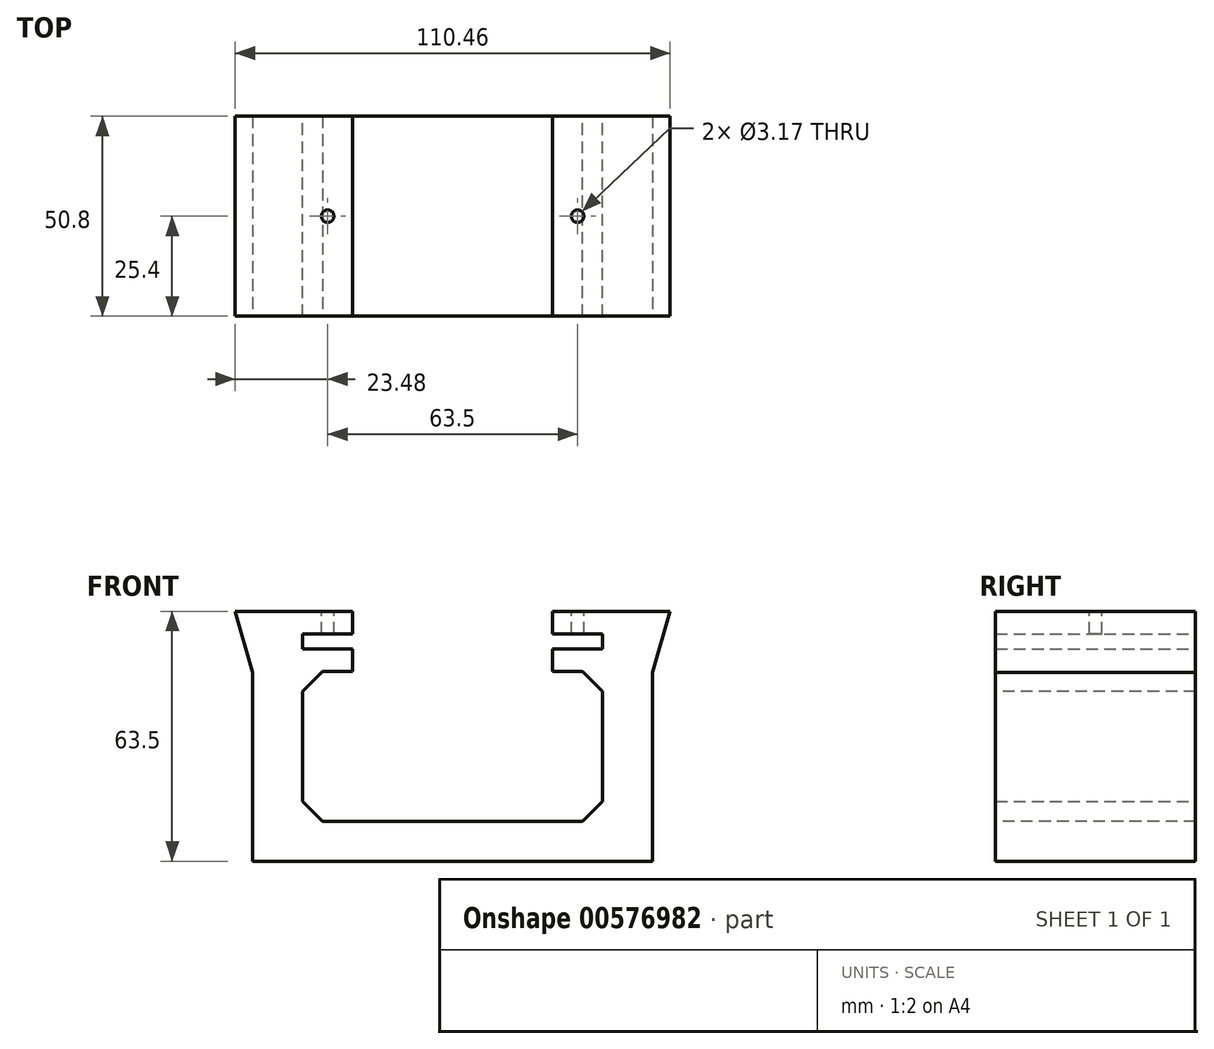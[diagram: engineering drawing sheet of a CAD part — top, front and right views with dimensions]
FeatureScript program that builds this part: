
annotation { "Feature Type Name" : "Feature", "Feature Type Description" : "" }
export const myFeature = defineFeature(function(context is Context, id is Id, definition is map)
    precondition{}
    {
        {
            var Q0;
            Q0=qCreatedBy(makeId("Front.planeOp"),FACE);
            var sketch = newSketch(context, id + "F0", { "sketchPlane" : qUnion([Q0])});
            skLineSegment(sketch, "E0.bottom", {"start": v(0, 0) * mm, "end": v(101.6, 0) * mm, "construction": true});
            skLineSegment(sketch, "E0.top", {"start": v(0, 63.5) * mm, "end": v(101.6, 63.5) * mm, "construction": true});
            skLineSegment(sketch, "E0.left", {"start": v(0, 0) * mm, "end": v(0, 63.5) * mm, "construction": true});
            skLineSegment(sketch, "E0.right", {"start": v(101.6, 0) * mm, "end": v(101.6, 63.5) * mm, "construction": true});
            skPoint(sketch, "E1", {"position": v(50.8, 63.5) * mm});
            skPoint(sketch, "E2", {"position": v(50.8, 0) * mm});
            skLineSegment(sketch, "E3", {"start": v(50.8, 63.5) * mm, "end": v(50.8, 0) * mm, "construction": true});
            skLineSegment(sketch, "E4.bottom", {"start": v(88.9, 53.98) * mm, "end": v(12.7, 53.97) * mm, "construction": true});
            skLineSegment(sketch, "E4.top", {"start": v(88.9, 57.79) * mm, "end": v(12.7, 57.79) * mm, "construction": true});
            skLineSegment(sketch, "E4.left", {"start": v(88.9, 53.98) * mm, "end": v(88.9, 57.79) * mm, "construction": true});
            skLineSegment(sketch, "E4.right", {"start": v(12.7, 53.97) * mm, "end": v(12.7, 57.79) * mm, "construction": true});
            skPoint(sketch, "E4.middle", {"position": v(50.8, 55.88) * mm});
            skLineSegment(sketch, "E5", {"start": v(25.4, 63.5) * mm, "end": v(25.4, 0) * mm, "construction": true});
            skLineSegment(sketch, "E6", {"start": v(0, 48.26) * mm, "end": v(101.6, 48.26) * mm, "construction": true});
            skLineSegment(sketch, "E7", {"start": v(25.4, 63.5) * mm, "end": v(0, 63.5) * mm});
            skLineSegment(sketch, "E8", {"start": v(0, 0) * mm, "end": v(50.8, 0) * mm});
            skLineSegment(sketch, "E9", {"start": v(50.8, 10.16) * mm, "end": v(12.7, 10.16) * mm});
            skLineSegment(sketch, "E10", {"start": v(12.7, 10.16) * mm, "end": v(12.7, 48.26) * mm});
            skLineSegment(sketch, "E11", {"start": v(12.7, 48.26) * mm, "end": v(25.4, 48.26) * mm});
            skLineSegment(sketch, "E12", {"start": v(25.4, 48.26) * mm, "end": v(25.4, 53.97) * mm});
            skLineSegment(sketch, "E13", {"start": v(25.4, 53.97) * mm, "end": v(12.7, 53.97) * mm});
            skLineSegment(sketch, "E14", {"start": v(12.7, 57.79) * mm, "end": v(25.4, 57.79) * mm});
            skLineSegment(sketch, "E15", {"start": v(25.4, 57.79) * mm, "end": v(25.4, 63.5) * mm});
            skLineSegment(sketch, "E16", {"start": v(12.7, 57.79) * mm, "end": v(12.7, 53.97) * mm});
            skLineSegment(sketch, "E17.MirrorCS", {"start": v(88.9, 53.97) * mm, "end": v(88.9, 57.78) * mm, "construction": true});
            skLineSegment(sketch, "E18.MirrorCS", {"start": v(88.9, 48.26) * mm, "end": v(76.2, 48.26) * mm});
            skLineSegment(sketch, "E19.MirrorCS", {"start": v(88.9, 10.16) * mm, "end": v(88.9, 48.26) * mm});
            skLineSegment(sketch, "E20.MirrorCS", {"start": v(76.2, 48.26) * mm, "end": v(76.2, 53.97) * mm});
            skLineSegment(sketch, "E21.MirrorCS", {"start": v(76.2, 53.97) * mm, "end": v(88.9, 53.97) * mm});
            skLineSegment(sketch, "E22.MirrorCS", {"start": v(50.8, 10.16) * mm, "end": v(88.9, 10.16) * mm});
            skLineSegment(sketch, "E23.MirrorCS", {"start": v(88.9, 57.78) * mm, "end": v(76.2, 57.78) * mm});
            skLineSegment(sketch, "E24.MirrorCS", {"start": v(88.9, 57.78) * mm, "end": v(88.9, 53.97) * mm});
            skLineSegment(sketch, "E25.MirrorCS", {"start": v(76.2, 57.78) * mm, "end": v(76.2, 63.5) * mm});
            skLineSegment(sketch, "E26.MirrorCS", {"start": v(101.6, 0) * mm, "end": v(50.8, 0) * mm});
            skLineSegment(sketch, "E27.MirrorCS", {"start": v(76.2, 63.5) * mm, "end": v(101.6, 63.5) * mm});
            skLineSegment(sketch, "E28.MirrorCS", {"start": v(76.2, 63.5) * mm, "end": v(76.2, 0) * mm, "construction": true});
            skLineSegment(sketch, "E29", {"start": v(0, 63.5) * mm, "end": v(0, 0) * mm});
            skLineSegment(sketch, "E30", {"start": v(101.6, 63.5) * mm, "end": v(101.6, 0) * mm});
            skSolve(sketch);
        }
        {
            var Q0;
            Q0=makeQuery(id+"F0.imprint","IMPRINT",FACE,{"disambiguationData":[TD([[makeQuery(id+"F0.imprint","IMPRINT",EDGE,{"derivedFrom":sQuery(id+"F0.wireOp",EDGE,"E7")}),1.0]])]});
            extrude(context, id + "F1", {"entities" : qUnion([Q0]), "depth" : 50.8 * mm, "offsetDistance" : 25.4 * mm});
        }
        {
            var Q0;
            Q0=makeQuery(id+"F1.opExtrude","SWEPT_FACE",FACE,{"disambiguationData":[OSD([sQuery(id+"F0.wireOp",EDGE,"E7")])]});
            var sketch = newSketch(context, id + "F2", { "sketchPlane" : qUnion([Q0])});
            skLineSegment(sketch, "E31", {"start": v(12.7, 0) * mm, "end": v(12.7, -50.8) * mm, "construction": true});
            skLineSegment(sketch, "E32", {"start": v(50.8, 0) * mm, "end": v(50.8, -50.58) * mm, "construction": true});
            skLineSegment(sketch, "E33", {"start": v(12.7, 0) * mm, "end": v(25.4, 0) * mm, "construction": true});
            skPoint(sketch, "E34", {"position": v(19.05, 0) * mm});
            skLineSegment(sketch, "E35", {"start": v(12.7, -50.8) * mm, "end": v(25.4, -50.8) * mm, "construction": true});
            skPoint(sketch, "E36", {"position": v(19.05, -50.8) * mm});
            skLineSegment(sketch, "E37", {"start": v(19.05, 0) * mm, "end": v(19.05, -50.8) * mm, "construction": true});
            skPoint(sketch, "E38", {"position": v(19.05, -25.4) * mm});
            skCircle(sketch, "E39", {"center": v(19.05, -25.4) * mm, "radius": 1.59 * mm});
            skCircle(sketch, "E40.MirrorC", {"center": v(82.55, -25.4) * mm, "radius": 1.59 * mm});
            skSolve(sketch);
        }
        {
            var Q0;
            Q0 = qSketchRegion(id + "F2", true);
            extrude(context, id + "F3", {"entities" : qUnion([Q0]), "operationType" : NewBodyOperationType.REMOVE, "endBound" : BoundingType.UP_TO_NEXT, "oppositeDirection" : true, "depth" : 25.4 * mm, "offsetDistance" : 25.4 * mm});
        }
        {
            var Q0;
            Q0=makeQuery(id+"F1.opExtrude","SWEPT_EDGE",EDGE,{"disambiguationData":[OSD([sQuery(id+"F0.wireOp",EDGE,"E9"),sQuery(id+"F0.wireOp",EDGE,"E10")])]});
            var Q1;
            Q1=makeQuery(id+"F1.opExtrude","SWEPT_EDGE",EDGE,{"disambiguationData":[OSD([sQuery(id+"F0.wireOp",EDGE,"E19.MirrorCS"),sQuery(id+"F0.wireOp",EDGE,"E22.MirrorCS")])]});
            var Q2;
            Q2=makeQuery(id+"F1.opExtrude","SWEPT_EDGE",EDGE,{"disambiguationData":[OSD([sQuery(id+"F0.wireOp",EDGE,"E10"),sQuery(id+"F0.wireOp",EDGE,"E11")])]});
            var Q3;
            Q3=makeQuery(id+"F1.opExtrude","SWEPT_EDGE",EDGE,{"disambiguationData":[OSD([sQuery(id+"F0.wireOp",EDGE,"E18.MirrorCS"),sQuery(id+"F0.wireOp",EDGE,"E19.MirrorCS")])]});
            chamfer(context, id + "F4", {"entities" : qUnion([Q0, Q1, Q2, Q3]), "width" : 5.08 * mm, "tangentPropagation" : true});
        }
        {
            var Q0;
            Q0=makeQuery(id+"F1.opExtrude","CAP_FACE",FACE,{"disambiguationData":[OSD([sQuery(id+"F0.wireOp",EDGE,"E7"),sQuery(id+"F0.wireOp",EDGE,"E8"),sQuery(id+"F0.wireOp",EDGE,"E9"),sQuery(id+"F0.wireOp",EDGE,"E10"),sQuery(id+"F0.wireOp",EDGE,"E11"),sQuery(id+"F0.wireOp",EDGE,"E12"),sQuery(id+"F0.wireOp",EDGE,"E13"),sQuery(id+"F0.wireOp",EDGE,"E14"),sQuery(id+"F0.wireOp",EDGE,"E15"),sQuery(id+"F0.wireOp",EDGE,"E16"),sQuery(id+"F0.wireOp",EDGE,"E18.MirrorCS"),sQuery(id+"F0.wireOp",EDGE,"E19.MirrorCS"),sQuery(id+"F0.wireOp",EDGE,"E20.MirrorCS"),sQuery(id+"F0.wireOp",EDGE,"E21.MirrorCS"),sQuery(id+"F0.wireOp",EDGE,"E22.MirrorCS"),sQuery(id+"F0.wireOp",EDGE,"E23.MirrorCS"),sQuery(id+"F0.wireOp",EDGE,"E24.MirrorCS"),sQuery(id+"F0.wireOp",EDGE,"E25.MirrorCS"),sQuery(id+"F0.wireOp",EDGE,"E26.MirrorCS"),sQuery(id+"F0.wireOp",EDGE,"E27.MirrorCS"),sQuery(id+"F0.wireOp",EDGE,"E29"),sQuery(id+"F0.wireOp",EDGE,"E30")])],"isStart":false});
            var sketch = newSketch(context, id + "F5", { "sketchPlane" : qUnion([Q0])});
            skLineSegment(sketch, "E41", {"start": v(0, 63.5) * mm, "end": v(-4.43, 63.5) * mm});
            skLineSegment(sketch, "E42", {"start": v(-4.43, 63.5) * mm, "end": v(0, 47.96) * mm});
            skLineSegment(sketch, "E43", {"start": v(0, 47.96) * mm, "end": v(0, 63.5) * mm});
            skLineSegment(sketch, "E44.MirrorCS", {"start": v(101.6, 47.96) * mm, "end": v(101.6, 63.5) * mm});
            skLineSegment(sketch, "E45.MirrorCS", {"start": v(101.6, 63.5) * mm, "end": v(106.03, 63.5) * mm});
            skLineSegment(sketch, "E46.MirrorCS", {"start": v(106.03, 63.5) * mm, "end": v(101.6, 47.96) * mm});
            skSolve(sketch);
        }
        {
            var Q0;
            Q0 = qSketchRegion(id + "F5", true);
            extrude(context, id + "F6", {"entities" : qUnion([Q0]), "operationType" : NewBodyOperationType.ADD, "oppositeDirection" : true, "depth" : 50.8 * mm, "offsetDistance" : 25.4 * mm});
        }
    });
